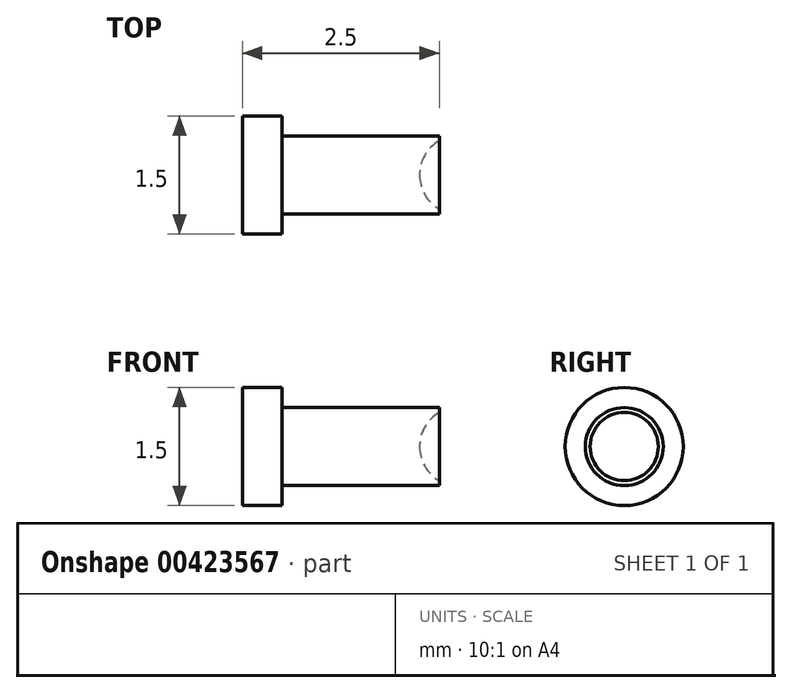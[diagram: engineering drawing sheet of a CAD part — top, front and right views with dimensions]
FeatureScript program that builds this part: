
annotation { "Feature Type Name" : "Feature", "Feature Type Description" : "" }
export const myFeature = defineFeature(function(context is Context, id is Id, definition is map)
    precondition{}
    {
        {
            var Q0;
            Q0=qCreatedBy(makeId("Front.planeOp"),FACE);
            var sketch = newSketch(context, id + "F0", { "sketchPlane" : qUnion([Q0])});
            skLineSegment(sketch, "E0", {"start": v(0, 0) * mm, "end": v(0, 0.75) * mm});
            skLineSegment(sketch, "E1", {"start": v(0, 0.75) * mm, "end": v(0.5, 0.75) * mm});
            skLineSegment(sketch, "E2", {"start": v(0.5, 0.75) * mm, "end": v(0.5, 0.5) * mm});
            skLineSegment(sketch, "E3", {"start": v(0.5, 0.5) * mm, "end": v(2.5, 0.5) * mm});
            skLineSegment(sketch, "E4", {"start": v(2.5, 0.5) * mm, "end": v(2.5, 0.43) * mm});
            skLineSegment(sketch, "E5", {"start": v(2.25, 0) * mm, "end": v(0, 0) * mm});
            skLineSegment(sketch, "E6", {"start": v(-0.3, 0) * mm, "end": v(1.55, 0) * mm, "construction": true});
            skArc(sketch, "E7", {"start": v(2.5, 0.43) * mm, "mid": v(2.32, 0.25) * mm, "end": v(2.25, 0) * mm});
            skPoint(sketch, "E8.orphan", {"position": v(2.5, 0) * mm});
            skSolve(sketch);
        }
        {
            var Q0;
            Q0=makeQuery(id+"F0.imprint","IMPRINT",FACE,{"disambiguationData":[TD([[makeQuery(id+"F0.imprint","IMPRINT",EDGE,{"derivedFrom":sQuery(id+"F0.wireOp",EDGE,"E0")}),-1.0]])]});
            var Q1;
            Q1=sQuery(id+"F0.wireOp",EDGE,"E6");
            revolve(context, id + "F1", {"entities" : qUnion([Q0]), "axis" : qUnion([Q1]), "revolveType" : RevolveType.FULL});
        }
    });
